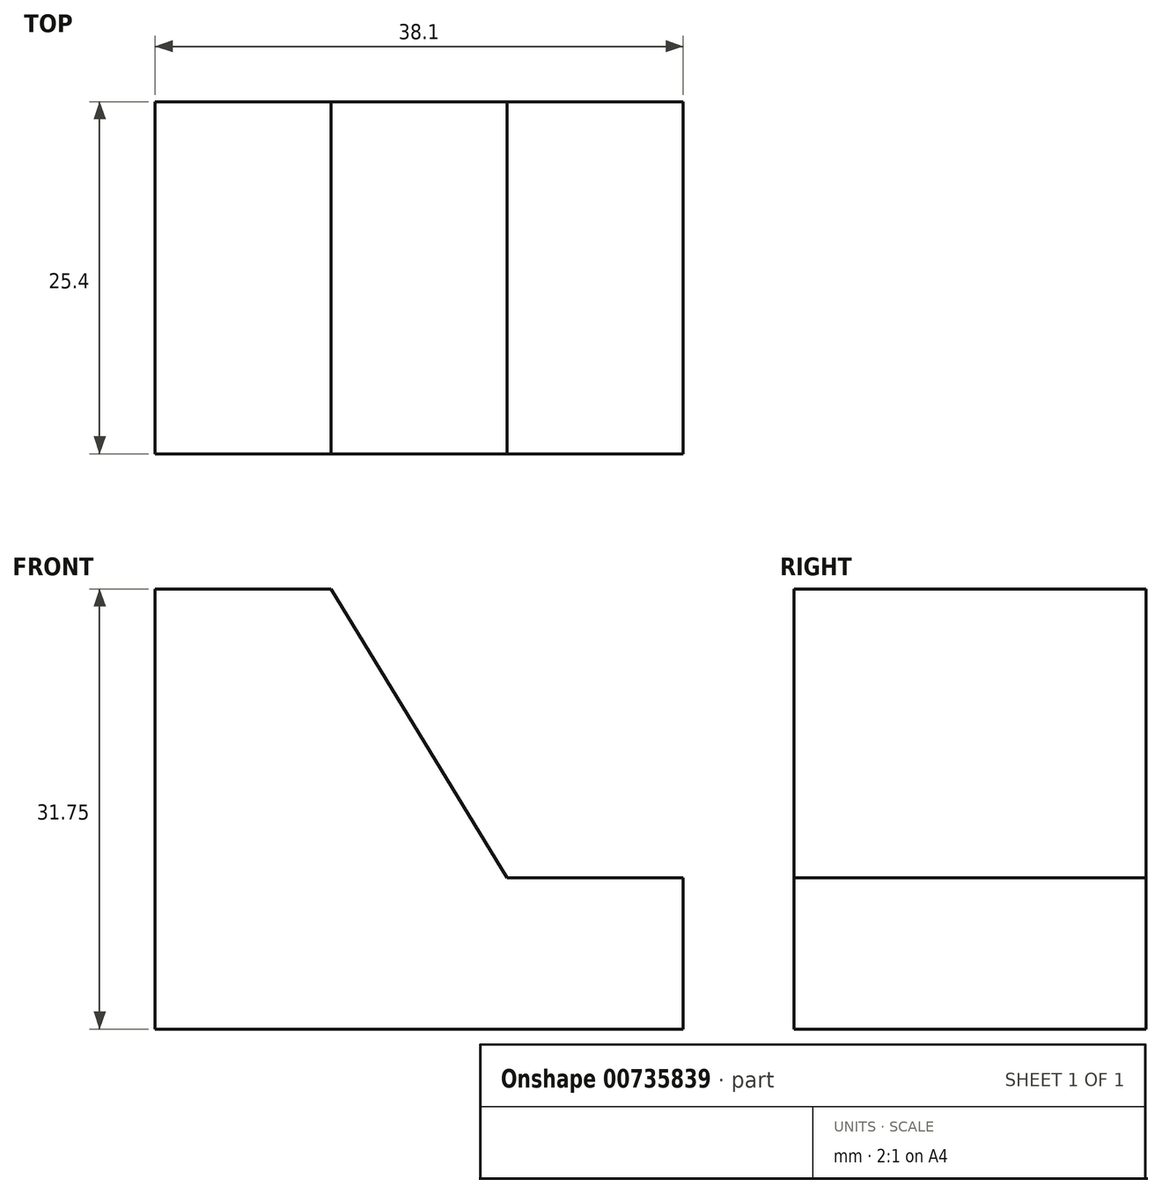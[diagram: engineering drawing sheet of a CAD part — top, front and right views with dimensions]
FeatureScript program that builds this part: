
annotation { "Feature Type Name" : "Feature", "Feature Type Description" : "" }
export const myFeature = defineFeature(function(context is Context, id is Id, definition is map)
    precondition{}
    {
        {
            var Q0;
            Q0=qCreatedBy(makeId("Front.planeOp"),FACE);
            var sketch = newSketch(context, id + "F0", { "sketchPlane" : qUnion([Q0])});
            skLineSegment(sketch, "E0", {"start": v(0, 0) * mm, "end": v(38.1, 0) * mm});
            skLineSegment(sketch, "E1", {"start": v(38.1, 0) * mm, "end": v(38.1, 31.75) * mm});
            skLineSegment(sketch, "E2", {"start": v(38.1, 31.75) * mm, "end": v(0, 31.75) * mm});
            skLineSegment(sketch, "E3", {"start": v(0, 31.75) * mm, "end": v(0, 0) * mm});
            skSolve(sketch);
        }
        {
            var Q0;
            Q0 = qSketchRegion(id + "F0", true);
            extrude(context, id + "F1", {"entities" : qUnion([Q0]), "depth" : 25.4 * mm, "offsetDistance" : 25.4 * mm});
        }
        {
            var Q0;
            Q0=makeQuery(id+"F1.opExtrude","CAP_FACE",FACE,{"disambiguationData":[OSD([sQuery(id+"F0.wireOp",EDGE,"E0"),sQuery(id+"F0.wireOp",EDGE,"E1"),sQuery(id+"F0.wireOp",EDGE,"E2"),sQuery(id+"F0.wireOp",EDGE,"E3")])],"isStart":true});
            var sketch = newSketch(context, id + "F2", { "sketchPlane" : qUnion([Q0])});
            skLineSegment(sketch, "E4", {"start": v(-12.7, 31.75) * mm, "end": v(-25.4, 10.92) * mm});
            skLineSegment(sketch, "E5", {"start": v(-25.4, 10.92) * mm, "end": v(-38.1, 10.92) * mm});
            skSolve(sketch);
        }
        {
            var Q0;
            Q0 = qSketchRegion(id + "F2", true);
            var Q1;
            {var subQ0=sQuery(id+"F2.wireOp",EDGE,"E4");Q1=makeQuery(id+"F2.imprint","IMPRINT",FACE,{"disambiguationData":[TD([[makeQuery(id+"F2.imprint","IMPRINT",EDGE,{"derivedFrom":subQ0}),-1.0]])]});}
            extrude(context, id + "F3", {"entities" : qUnion([Q0, Q1]), "operationType" : NewBodyOperationType.REMOVE, "oppositeDirection" : true, "depth" : 25.4 * mm, "offsetDistance" : 25.4 * mm});
        }
    });
